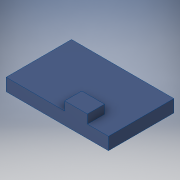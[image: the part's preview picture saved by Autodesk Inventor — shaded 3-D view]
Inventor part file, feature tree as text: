
AUTODESK INVENTOR PART (.ipt)
format: ipt  version: 2018 (Build 220112000, 112)  size: 119,296 bytes
history: native  units: in
note: dims shown in document units (in); Inventor stores cm internally (conversion verified against a paired STEP export)
features: extrude x2, sketch x2
ambient origin geometry x8: Origin, YZ Plane, XZ Plane, XY Plane, X Axis, Y Axis, Z Axis, Center Point
bodies: Solid1 (feature_tree)
feature tree (4):
  extrude  "Extrusion1"  Depth=0.9055in
  extrude  "Extrusion2"  Depth=0.315in
  sketch  "Sketch1"  dims[d0=1.4173in d1=0.9055in]
  sketch  "Sketch2"  dims[d2=0.1732in d3=0.0in d4=0.315in d5=0.2362in d6=0.2913in d7=0.122in d8=0.0in]
